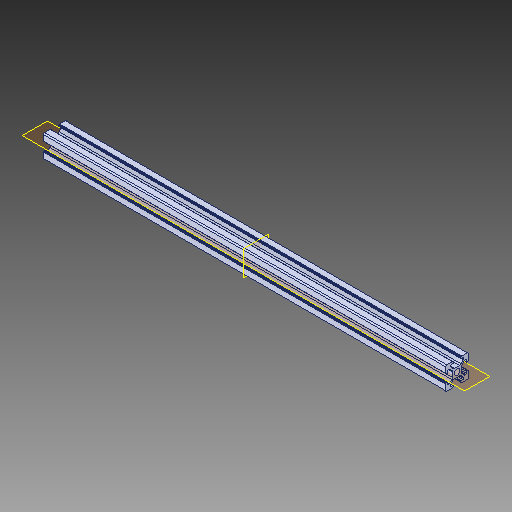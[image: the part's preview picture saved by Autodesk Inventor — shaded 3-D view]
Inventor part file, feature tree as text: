
AUTODESK INVENTOR PART (.ipt)
format: ipt  version: 2018 (Build 220112000, 112)  size: 371,712 bytes
history: native  units: in
note: dims shown in document units (in); Inventor stores cm internally (conversion verified against a paired STEP export)
features: extrude x1, plane x1, sketch x1, projected_geometry x1, fillet x1
ambient origin geometry x8: Origin, YZ Plane, XZ Plane, XY Plane, X Axis, Y Axis, Z Axis, Center Point
bodies: Solid1 (feature_tree)
feature tree (5):
  extrude  "Extrusion2"  [1 undecoded]
  plane  "Work Plane1"
  sketch  "Sketch3"  dims[d2=9.8425in d3=0.0in]
  projected_geometry  "Projected Loop2"
  fillet  "Fillet5"  [1 undecoded]
note: 2 required parameter values undecoded (feature->parameter linkage not recoverable at this tier; creation-order binding heuristic only, values carry confidence <= 0.55)
